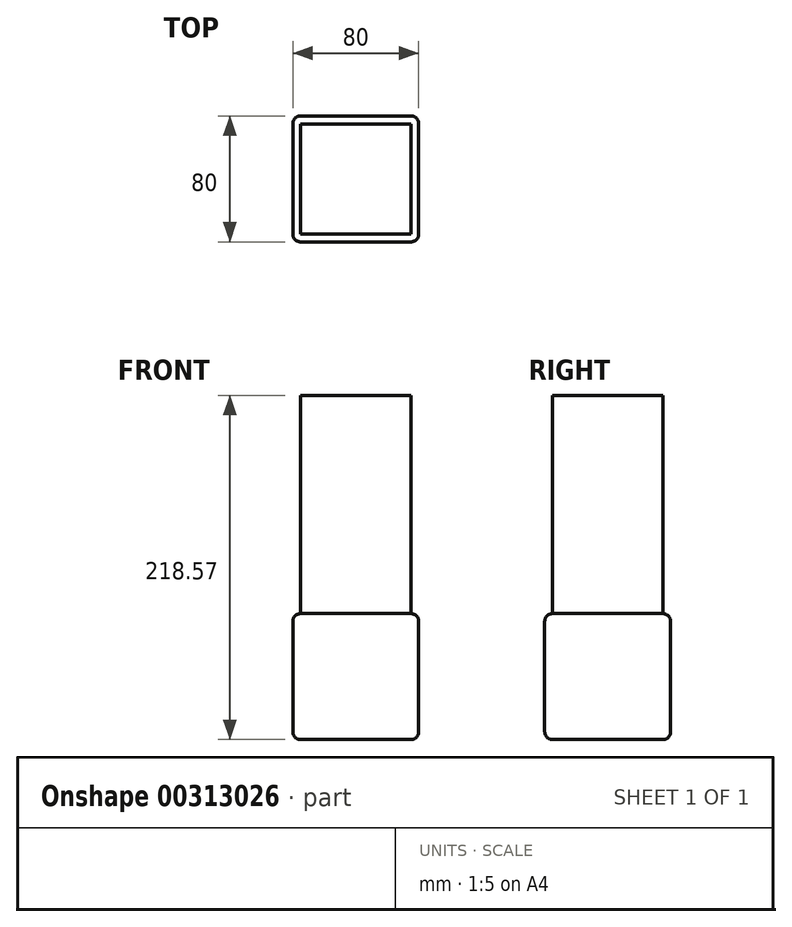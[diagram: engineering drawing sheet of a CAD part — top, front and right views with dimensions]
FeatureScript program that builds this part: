
annotation { "Feature Type Name" : "Feature", "Feature Type Description" : "" }
export const myFeature = defineFeature(function(context is Context, id is Id, definition is map)
    precondition{}
    {
        {
            var Q0;
            Q0=qCreatedBy(makeId("Top.planeOp"),FACE);
            var sketch = newSketch(context, id + "F0", { "sketchPlane" : qUnion([Q0])});
            skLineSegment(sketch, "E0.bottom", {"start": v(-40, 40) * mm, "end": v(40, 40) * mm});
            skLineSegment(sketch, "E0.top", {"start": v(-40, -40) * mm, "end": v(40, -40) * mm});
            skLineSegment(sketch, "E0.left", {"start": v(-40, 40) * mm, "end": v(-40, -40) * mm});
            skLineSegment(sketch, "E0.right", {"start": v(40, 40) * mm, "end": v(40, -40) * mm});
            skPoint(sketch, "E0.middle", {"position": v(0, 0) * mm});
            skSolve(sketch);
        }
        {
            var Q0;
            Q0=makeQuery(id+"F0.imprint","IMPRINT",FACE,{"disambiguationData":[TD([[makeQuery(id+"F0.imprint","IMPRINT",EDGE,{"derivedFrom":sQuery(id+"F0.wireOp",EDGE,"E0.bottom")}),-1.0]])]});
            extrude(context, id + "F1", {"entities" : qUnion([Q0]), "endBound" : BoundingType.SYMMETRIC, "depth" : 80 * mm});
        }
        {
            var Q0;
            Q0=makeQuery(id+"F1.opExtrude","CAP_EDGE",EDGE,{"disambiguationData":[OSD([sQuery(id+"F0.wireOp",EDGE,"E0.bottom")])],"isStart":false});
            var Q1;
            Q1=makeQuery(id+"F1.opExtrude","CAP_EDGE",EDGE,{"disambiguationData":[OSD([sQuery(id+"F0.wireOp",EDGE,"E0.left")])],"isStart":false});
            var Q2;
            Q2=makeQuery(id+"F1.opExtrude","CAP_EDGE",EDGE,{"disambiguationData":[OSD([sQuery(id+"F0.wireOp",EDGE,"E0.right")])],"isStart":false});
            var Q3;
            Q3=makeQuery(id+"F1.opExtrude","CAP_EDGE",EDGE,{"disambiguationData":[OSD([sQuery(id+"F0.wireOp",EDGE,"E0.top")])],"isStart":false});
            var Q4;
            Q4=makeQuery(id+"F1.opExtrude","SWEPT_EDGE",EDGE,{"disambiguationData":[OSD([sQuery(id+"F0.wireOp",EDGE,"E0.bottom"),sQuery(id+"F0.wireOp",EDGE,"E0.right")])]});
            var Q5;
            Q5=makeQuery(id+"F1.opExtrude","SWEPT_EDGE",EDGE,{"disambiguationData":[OSD([sQuery(id+"F0.wireOp",EDGE,"E0.top"),sQuery(id+"F0.wireOp",EDGE,"E0.right")])]});
            var Q6;
            Q6=makeQuery(id+"F1.opExtrude","CAP_EDGE",EDGE,{"disambiguationData":[OSD([sQuery(id+"F0.wireOp",EDGE,"E0.right")])],"isStart":true});
            var Q7;
            Q7=makeQuery(id+"F1.opExtrude","SWEPT_EDGE",EDGE,{"disambiguationData":[OSD([sQuery(id+"F0.wireOp",EDGE,"E0.bottom"),sQuery(id+"F0.wireOp",EDGE,"E0.left")])]});
            var Q8;
            Q8=makeQuery(id+"F1.opExtrude","SWEPT_FACE",FACE,{"disambiguationData":[OSD([sQuery(id+"F0.wireOp",EDGE,"E0.left")])]});
            var Q9;
            Q9=makeQuery(id+"F1.opExtrude","SWEPT_EDGE",EDGE,{"disambiguationData":[OSD([sQuery(id+"F0.wireOp",EDGE,"E0.top"),sQuery(id+"F0.wireOp",EDGE,"E0.left")])]});
            var Q10;
            Q10=makeQuery(id+"F1.opExtrude","CAP_EDGE",EDGE,{"disambiguationData":[OSD([sQuery(id+"F0.wireOp",EDGE,"E0.left")])],"isStart":true});
            var Q11;
            Q11=makeQuery(id+"F1.opExtrude","CAP_EDGE",EDGE,{"disambiguationData":[OSD([sQuery(id+"F0.wireOp",EDGE,"E0.top")])],"isStart":true});
            var Q12;
            Q12=makeQuery(id+"F1.opExtrude","CAP_EDGE",EDGE,{"disambiguationData":[OSD([sQuery(id+"F0.wireOp",EDGE,"E0.bottom")])],"isStart":true});
            fillet(context, id + "F2", {"entities" : qUnion([Q0, Q1, Q2, Q3, Q4, Q5, Q6, Q7, Q8, Q9, Q10, Q11, Q12]), "radius" : 5 * mm, "tangentPropagation" : true, "allowEdgeOverflow" : false});
        }
        {
            var Q0;
            Q0=makeQuery(id+"F1.opExtrude","CAP_FACE",FACE,{"disambiguationData":[OSD([sQuery(id+"F0.wireOp",EDGE,"E0.bottom"),sQuery(id+"F0.wireOp",EDGE,"E0.top"),sQuery(id+"F0.wireOp",EDGE,"E0.left"),sQuery(id+"F0.wireOp",EDGE,"E0.right")])],"isStart":true});
            var Q1;
            Q1=makeQuery(id+"F1.opExtrude","CAP_FACE",FACE,{"disambiguationData":[OSD([sQuery(id+"F0.wireOp",EDGE,"E0.bottom"),sQuery(id+"F0.wireOp",EDGE,"E0.top"),sQuery(id+"F0.wireOp",EDGE,"E0.left"),sQuery(id+"F0.wireOp",EDGE,"E0.right")])],"isStart":false});
            extrude(context, id + "F3", {"entities" : qUnion([Q0, Q1]), "operationType" : NewBodyOperationType.ADD, "endBound" : BoundingType.THROUGH_ALL, "oppositeDirection" : true, "depth" : 25 * mm});
        }
    });
